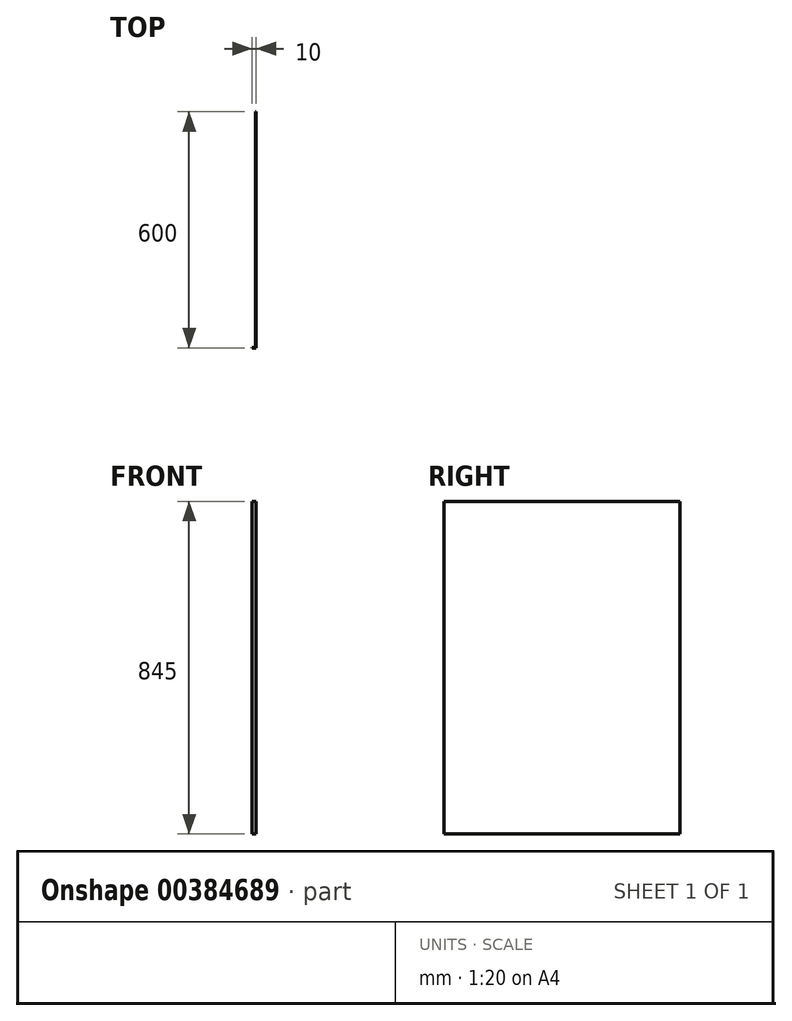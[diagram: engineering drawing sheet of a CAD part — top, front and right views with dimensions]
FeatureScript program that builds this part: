
annotation { "Feature Type Name" : "Feature", "Feature Type Description" : "" }
export const myFeature = defineFeature(function(context is Context, id is Id, definition is map)
    precondition{}
    {
        {
            var Q0;
            Q0=qCreatedBy(makeId("Top.planeOp"),FACE);
            var sketch = newSketch(context, id + "F0", { "sketchPlane" : qUnion([Q0])});
            skLineSegment(sketch, "E0", {"start": v(0, 0) * mm, "end": v(0, -600) * mm});
            skLineSegment(sketch, "E1", {"start": v(0, -600) * mm, "end": v(-10, -600) * mm});
            skLineSegment(sketch, "E2", {"start": v(-10, -600) * mm, "end": v(-10, -599) * mm});
            skLineSegment(sketch, "E3", {"start": v(-10, -599) * mm, "end": v(-1, -599) * mm});
            skLineSegment(sketch, "E4", {"start": v(-1, -599) * mm, "end": v(-1, 0) * mm});
            skLineSegment(sketch, "E5", {"start": v(-1, 0) * mm, "end": v(0, 0) * mm});
            skSolve(sketch);
        }
        {
            var Q0;
            Q0 = qSketchRegion(id + "F0", true);
            extrude(context, id + "F1", {"entities" : qUnion([Q0]), "depth" : 845 * mm});
        }
    });
